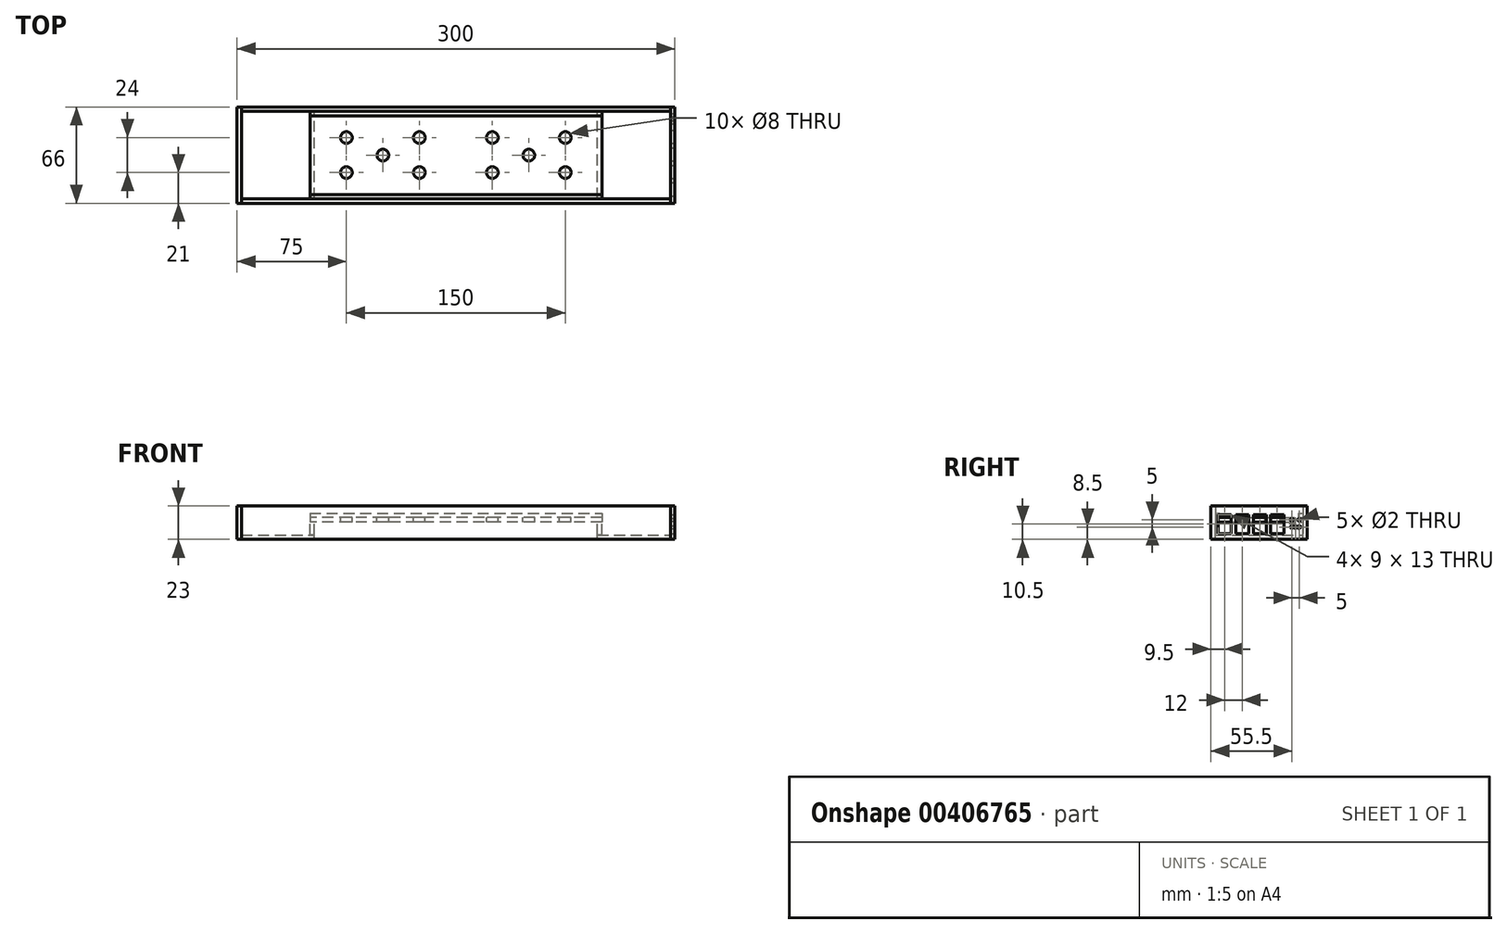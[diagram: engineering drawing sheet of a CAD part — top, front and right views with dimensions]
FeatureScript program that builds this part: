
annotation { "Feature Type Name" : "Feature", "Feature Type Description" : "" }
export const myFeature = defineFeature(function(context is Context, id is Id, definition is map)
    precondition{}
    {
        {
            var Q0;
            Q0=qCreatedBy(makeId("Top.planeOp"),FACE);
            var sketch = newSketch(context, id + "F0", { "sketchPlane" : qUnion([Q0])});
            skLineSegment(sketch, "E0.bottom", {"start": v(100, -30) * mm, "end": v(-100, -30) * mm});
            skLineSegment(sketch, "E0.top", {"start": v(100, 30) * mm, "end": v(-100, 30) * mm});
            skLineSegment(sketch, "E0.left", {"start": v(100, -30) * mm, "end": v(100, 30) * mm});
            skLineSegment(sketch, "E0.right", {"start": v(-100, -30) * mm, "end": v(-100, 30) * mm});
            skPoint(sketch, "E0.middle", {"position": v(0, 0) * mm});
            skSolve(sketch);
        }
        {
            var Q0;
            Q0=makeQuery(id+"F0.imprint","IMPRINT",FACE,{"disambiguationData":[TD([[makeQuery(id+"F0.imprint","IMPRINT",EDGE,{"derivedFrom":sQuery(id+"F0.wireOp",EDGE,"E0.bottom")}),-1.0]])]});
            extrude(context, id + "F1", {"entities" : qUnion([Q0]), "depth" : 3 * mm});
        }
        {
            var Q0;
            Q0=makeQuery(id+"F1.opExtrude","CAP_FACE",FACE,{"disambiguationData":[OSD([sQuery(id+"F0.wireOp",EDGE,"E0.bottom"),sQuery(id+"F0.wireOp",EDGE,"E0.top"),sQuery(id+"F0.wireOp",EDGE,"E0.left"),sQuery(id+"F0.wireOp",EDGE,"E0.right")])],"isStart":true});
            var sketch = newSketch(context, id + "F2", { "sketchPlane" : qUnion([Q0])});
            skLineSegment(sketch, "E1", {"start": v(-97, 30) * mm, "end": v(-97, -30) * mm});
            skLineSegment(sketch, "E2", {"start": v(97, 30) * mm, "end": v(97, -30) * mm});
            skSolve(sketch);
        }
        {
            var Q0;
            {var subQ0=sQuery(id+"F2.wireOp",EDGE,"E1");Q0=makeQuery(id+"F2.imprint","IMPRINT",FACE,{"disambiguationData":[TD([[makeQuery(id+"F2.imprint","IMPRINT",EDGE,{"derivedFrom":subQ0}),-1.0]])]});}
            var Q1;
            {var subQ0=sQuery(id+"F2.wireOp",EDGE,"E2");Q1=makeQuery(id+"F2.imprint","IMPRINT",FACE,{"disambiguationData":[TD([[makeQuery(id+"F2.imprint","IMPRINT",EDGE,{"derivedFrom":subQ0}),1.0]])]});}
            extrude(context, id + "F3", {"entities" : qUnion([Q0, Q1]), "depth" : 9 * mm});
        }
        {
            var Q0;
            Q0=makeQuery(id+"F3.opExtrude","CAP_FACE",FACE,{"disambiguationData":[OSD([sQuery(id+"F0.wireOp",EDGE,"E0.bottom"),sQuery(id+"F0.wireOp",EDGE,"E0.top"),sQuery(id+"F0.wireOp",EDGE,"E0.left"),sQuery(id+"F2.wireOp",EDGE,"E2")])],"isStart":false});
            var sketch = newSketch(context, id + "F4", { "sketchPlane" : qUnion([Q0])});
            skLineSegment(sketch, "E3", {"start": v(97, 30) * mm, "end": v(147, 30) * mm});
            skLineSegment(sketch, "E4", {"start": v(147, 30) * mm, "end": v(147, -30) * mm});
            skLineSegment(sketch, "E5", {"start": v(147, -30) * mm, "end": v(97, -30) * mm});
            skSolve(sketch);
        }
        {
            var Q0;
            {var subQ2=sQuery(id+"F4.wireOp",EDGE,"E4");Q0=makeQuery(id+"F4.imprint","IMPRINT",FACE,{"disambiguationData":[TD([[makeQuery(id+"F4.imprint","IMPRINT",EDGE,{"derivedFrom":subQ2}),-1.0]])]});}
            var Q1;
            {var subQ2=makeQuery(id+"F3.opExtrude","CAP_EDGE",EDGE,{"disambiguationData":[OSD([sQuery(id+"F2.wireOp",EDGE,"E2")])],"isStart":false});Q1=makeQuery(id+"F4.imprint","IMPRINT",FACE,{"disambiguationData":[TD([[makeQuery(id+"F4.imprint","IMPRINT",EDGE,{"derivedFrom":subQ2}),1.0]])]});}
            extrude(context, id + "F5", {"entities" : qUnion([Q0, Q1]), "depth" : 3 * mm});
        }
        {
            var Q0;
            Q0=makeQuery(id+"F3.opExtrude","CAP_FACE",FACE,{"disambiguationData":[OSD([sQuery(id+"F0.wireOp",EDGE,"E0.bottom"),sQuery(id+"F0.wireOp",EDGE,"E0.top"),sQuery(id+"F0.wireOp",EDGE,"E0.right"),sQuery(id+"F2.wireOp",EDGE,"E1")])],"isStart":false});
            var sketch = newSketch(context, id + "F6", { "sketchPlane" : qUnion([Q0])});
            skLineSegment(sketch, "E6", {"start": v(-97, 30) * mm, "end": v(-147, 30) * mm});
            skLineSegment(sketch, "E7", {"start": v(-147, 30) * mm, "end": v(-147, -30) * mm});
            skLineSegment(sketch, "E8", {"start": v(-147, -30) * mm, "end": v(-97, -30) * mm});
            skSolve(sketch);
        }
        {
            var Q0;
            {var subQ2=sQuery(id+"F6.wireOp",EDGE,"E7");Q0=makeQuery(id+"F6.imprint","IMPRINT",FACE,{"disambiguationData":[TD([[makeQuery(id+"F6.imprint","IMPRINT",EDGE,{"derivedFrom":subQ2}),1.0]])]});}
            var Q1;
            {var subQ2=makeQuery(id+"F3.opExtrude","CAP_EDGE",EDGE,{"disambiguationData":[OSD([sQuery(id+"F2.wireOp",EDGE,"E1")])],"isStart":false});Q1=makeQuery(id+"F6.imprint","IMPRINT",FACE,{"disambiguationData":[TD([[makeQuery(id+"F6.imprint","IMPRINT",EDGE,{"derivedFrom":subQ2}),-1.0]])]});}
            extrude(context, id + "F7", {"entities" : qUnion([Q0, Q1]), "depth" : 3 * mm});
        }
        {
            var Q0;
            Q0=makeQuery(id+"F1.opExtrude","CAP_FACE",FACE,{"disambiguationData":[OSD([sQuery(id+"F0.wireOp",EDGE,"E0.bottom"),sQuery(id+"F0.wireOp",EDGE,"E0.top"),sQuery(id+"F0.wireOp",EDGE,"E0.left"),sQuery(id+"F0.wireOp",EDGE,"E0.right")])],"isStart":false});
            var sketch = newSketch(context, id + "F8", { "sketchPlane" : qUnion([Q0])});
            skLineSegment(sketch, "E9", {"start": v(-100, 27) * mm, "end": v(100, 27) * mm});
            skLineSegment(sketch, "E10", {"start": v(-100, -27) * mm, "end": v(100, -27) * mm});
            skSolve(sketch);
        }
        {
            var Q0;
            {var subQ0=sQuery(id+"F8.wireOp",EDGE,"E9");Q0=makeQuery(id+"F8.imprint","IMPRINT",FACE,{"disambiguationData":[TD([[makeQuery(id+"F8.imprint","IMPRINT",EDGE,{"derivedFrom":subQ0}),1.0]])]});}
            var Q1;
            {var subQ0=sQuery(id+"F8.wireOp",EDGE,"E10");Q1=makeQuery(id+"F8.imprint","IMPRINT",FACE,{"disambiguationData":[TD([[makeQuery(id+"F8.imprint","IMPRINT",EDGE,{"derivedFrom":subQ0}),-1.0]])]});}
            extrude(context, id + "F9", {"entities" : qUnion([Q0, Q1]), "depth" : 3 * mm});
        }
        {
            var Q0;
            Q0=makeQuery(id+"F1.opExtrude","CAP_FACE",FACE,{"disambiguationData":[OSD([sQuery(id+"F0.wireOp",EDGE,"E0.bottom"),sQuery(id+"F0.wireOp",EDGE,"E0.top"),sQuery(id+"F0.wireOp",EDGE,"E0.left"),sQuery(id+"F0.wireOp",EDGE,"E0.right")])],"isStart":false});
            var sketch = newSketch(context, id + "F10", { "sketchPlane" : qUnion([Q0])});
            skLineSegment(sketch, "E11", {"start": v(0, 30) * mm, "end": v(0, -30) * mm, "construction": true});
            skLineSegment(sketch, "E12", {"start": v(-100, 0) * mm, "end": v(100, 0) * mm, "construction": true});
            skLineSegment(sketch, "E13", {"start": v(-25, 30) * mm, "end": v(-25, -30) * mm, "construction": true});
            skLineSegment(sketch, "E14", {"start": v(-75, 30) * mm, "end": v(-75, -30) * mm, "construction": true});
            skLineSegment(sketch, "E15", {"start": v(25, 30) * mm, "end": v(25, -30) * mm, "construction": true});
            skLineSegment(sketch, "E16", {"start": v(75, 30) * mm, "end": v(75, -30) * mm, "construction": true});
            skLineSegment(sketch, "E17", {"start": v(-100, 12) * mm, "end": v(100, 12) * mm, "construction": true});
            skLineSegment(sketch, "E18", {"start": v(-100, -12) * mm, "end": v(100, -12) * mm, "construction": true});
            skLineSegment(sketch, "E19", {"start": v(50, 30) * mm, "end": v(50, -30) * mm, "construction": true});
            skCircle(sketch, "E20", {"center": v(-75, 12) * mm, "radius": 10 * mm, "construction": true});
            skCircle(sketch, "E21", {"center": v(-75, -12) * mm, "radius": 10 * mm, "construction": true});
            skCircle(sketch, "E22", {"center": v(-50, 0) * mm, "radius": 10 * mm, "construction": true});
            skCircle(sketch, "E23", {"center": v(-25, 12) * mm, "radius": 10 * mm, "construction": true});
            skCircle(sketch, "E24", {"center": v(-25, -12) * mm, "radius": 10 * mm, "construction": true});
            skCircle(sketch, "E25", {"center": v(25, 12) * mm, "radius": 10 * mm, "construction": true});
            skPoint(sketch, "E25.centerSnap0", {"position": v(25, 0) * mm});
            skCircle(sketch, "E26", {"center": v(25, -12) * mm, "radius": 10 * mm, "construction": true});
            skCircle(sketch, "E27", {"center": v(75, 12) * mm, "radius": 10 * mm, "construction": true});
            skCircle(sketch, "E28", {"center": v(75, -12) * mm, "radius": 10 * mm, "construction": true});
            skCircle(sketch, "E29", {"center": v(50, 0) * mm, "radius": 10 * mm, "construction": true});
            skCircle(sketch, "E30", {"center": v(75, 12) * mm, "radius": 4 * mm});
            skCircle(sketch, "E31", {"center": v(75, -12) * mm, "radius": 4 * mm});
            skCircle(sketch, "E32", {"center": v(50, 0) * mm, "radius": 4 * mm});
            skCircle(sketch, "E33", {"center": v(25, 12) * mm, "radius": 4 * mm});
            skCircle(sketch, "E34", {"center": v(25, -12) * mm, "radius": 4 * mm});
            skCircle(sketch, "E35", {"center": v(-25, 12) * mm, "radius": 4 * mm});
            skCircle(sketch, "E36", {"center": v(-25, -12) * mm, "radius": 4 * mm});
            skCircle(sketch, "E37", {"center": v(-50, 0) * mm, "radius": 4 * mm});
            skCircle(sketch, "E38", {"center": v(-75, 12) * mm, "radius": 4 * mm});
            skCircle(sketch, "E39", {"center": v(-75, -12) * mm, "radius": 4 * mm});
            skLineSegment(sketch, "E40", {"start": v(-50, 30) * mm, "end": v(-50, -30) * mm, "construction": true});
            skSolve(sketch);
        }
        {
            var Q0;
            Q0=makeQuery(id+"F10.imprint","IMPRINT",FACE,{"disambiguationData":[TD([[makeQuery(id+"F10.imprint","IMPRINT",EDGE,{"derivedFrom":sQuery(id+"F10.wireOp",EDGE,"E38")}),1.0]])]});
            var Q1;
            Q1=makeQuery(id+"F10.imprint","IMPRINT",FACE,{"disambiguationData":[TD([[makeQuery(id+"F10.imprint","IMPRINT",EDGE,{"derivedFrom":sQuery(id+"F10.wireOp",EDGE,"E39")}),1.0]])]});
            var Q2;
            Q2=makeQuery(id+"F10.imprint","IMPRINT",FACE,{"disambiguationData":[TD([[makeQuery(id+"F10.imprint","IMPRINT",EDGE,{"derivedFrom":sQuery(id+"F10.wireOp",EDGE,"E36")}),1.0]])]});
            var Q3;
            Q3=makeQuery(id+"F10.imprint","IMPRINT",FACE,{"disambiguationData":[TD([[makeQuery(id+"F10.imprint","IMPRINT",EDGE,{"derivedFrom":sQuery(id+"F10.wireOp",EDGE,"E35")}),1.0]])]});
            var Q4;
            Q4=makeQuery(id+"F10.imprint","IMPRINT",FACE,{"disambiguationData":[TD([[makeQuery(id+"F10.imprint","IMPRINT",EDGE,{"derivedFrom":sQuery(id+"F10.wireOp",EDGE,"E33")}),1.0]])]});
            var Q5;
            Q5=makeQuery(id+"F10.imprint","IMPRINT",FACE,{"disambiguationData":[TD([[makeQuery(id+"F10.imprint","IMPRINT",EDGE,{"derivedFrom":sQuery(id+"F10.wireOp",EDGE,"E34")}),1.0]])]});
            var Q6;
            Q6=makeQuery(id+"F10.imprint","IMPRINT",FACE,{"disambiguationData":[TD([[makeQuery(id+"F10.imprint","IMPRINT",EDGE,{"derivedFrom":sQuery(id+"F10.wireOp",EDGE,"E32")}),1.0]])]});
            var Q7;
            Q7=makeQuery(id+"F10.imprint","IMPRINT",FACE,{"disambiguationData":[TD([[makeQuery(id+"F10.imprint","IMPRINT",EDGE,{"derivedFrom":sQuery(id+"F10.wireOp",EDGE,"E30")}),1.0]])]});
            var Q8;
            Q8=makeQuery(id+"F10.imprint","IMPRINT",FACE,{"disambiguationData":[TD([[makeQuery(id+"F10.imprint","IMPRINT",EDGE,{"derivedFrom":sQuery(id+"F10.wireOp",EDGE,"E31")}),1.0]])]});
            var Q9;
            {var subQ0=sQuery(id+"F10.wireOp",EDGE,"E37");var subQ1=sQuery(id+"F10.wireOp",EDGE,"U7lCM9GL-lPuP-iNZp-IQAg-3zTcT3e2uVGl");var subQ2=makeQuery(id+"F10.imprint","INTERSECT",VERTEX,{"disambiguationData":[OD(0.0)],"derivedFrom":[subQ1,subQ0]});Q9=makeQuery(id+"F10.imprint","IMPRINT",FACE,{"disambiguationData":[TD([[makeQuery(id+"F10.imprint","IMPRINT",EDGE,{"disambiguationData":[TD([[subQ2,-1.0]])],"derivedFrom":subQ1}),1.0]])]});}
            var Q10;
            {var subQ0=sQuery(id+"F10.wireOp",EDGE,"E37");var subQ1=sQuery(id+"F10.wireOp",EDGE,"U7lCM9GL-lPuP-iNZp-IQAg-3zTcT3e2uVGl");var subQ2=makeQuery(id+"F10.imprint","INTERSECT",VERTEX,{"disambiguationData":[OD(0.0)],"derivedFrom":[subQ1,subQ0]});Q10=makeQuery(id+"F10.imprint","IMPRINT",FACE,{"disambiguationData":[TD([[makeQuery(id+"F10.imprint","IMPRINT",EDGE,{"disambiguationData":[TD([[subQ2,-1.0]])],"derivedFrom":subQ1}),-1.0]])]});}
            var Q11;
            Q11=makeQuery(id+"F10.imprint","IMPRINT",FACE,{"disambiguationData":[TD([[makeQuery(id+"F10.imprint","IMPRINT",EDGE,{"derivedFrom":sQuery(id+"F10.wireOp",EDGE,"E37")}),1.0]])]});
            extrude(context, id + "F11", {"entities" : qUnion([Q0, Q1, Q2, Q3, Q4, Q5, Q6, Q7, Q8, Q9, Q10, Q11]), "operationType" : NewBodyOperationType.REMOVE, "oppositeDirection" : true, "depth" : 3 * mm});
        }
        {
            var Q0;
            Q0=makeQuery(id+"F1.opExtrude","SWEPT_FACE",FACE,{"disambiguationData":[OSD([sQuery(id+"F0.wireOp",EDGE,"E0.bottom")])]});
            var sketch = newSketch(context, id + "F12", { "sketchPlane" : qUnion([Q0])});
            skLineSegment(sketch, "E41.bottom", {"start": v(-147, 11) * mm, "end": v(147, 11) * mm});
            skLineSegment(sketch, "E41.top", {"start": v(-147, -12) * mm, "end": v(147, -12) * mm});
            skLineSegment(sketch, "E41.left", {"start": v(-147, 11) * mm, "end": v(-147, -12) * mm});
            skLineSegment(sketch, "E41.right", {"start": v(147, 11) * mm, "end": v(147, -12) * mm});
            skLineSegment(sketch, "E42", {"start": v(0, 28.89) * mm, "end": v(0, -38.06) * mm, "construction": true});
            skPoint(sketch, "E42.startSnap0", {"position": v(0, 3) * mm});
            skLineSegment(sketch, "E43", {"start": v(164.78, 0) * mm, "end": v(-162.43, 0) * mm, "construction": true});
            skPoint(sketch, "E43.startSnap0", {"position": v(0, 0) * mm});
            skPoint(sketch, "E43.endSnap0", {"position": v(0, 0) * mm});
            skSolve(sketch);
        }
        {
            var Q0;
            Q0=makeQuery(id+"F12.imprint","IMPRINT",FACE,{"disambiguationData":[TD([[makeQuery(id+"F12.imprint","IMPRINT",EDGE,{"derivedFrom":sQuery(id+"F12.wireOp",EDGE,"E41.bottom")}),-1.0]])]});
            var Q1;
            {var subQ0=sQuery(id+"F0.wireOp",EDGE,"E0.bottom");Q1=makeQuery(id+"F12.imprint","IMPRINT",FACE,{"disambiguationData":[TD([[makeQuery(id+"F12.imprint","IMPRINT",EDGE,{"derivedFrom":makeQuery(id+"F1.opExtrude","CAP_EDGE",EDGE,{"disambiguationData":[OSD([subQ0])],"isStart":true})}),-1.0]])]});}
            extrude(context, id + "F13", {"entities" : qUnion([Q0, Q1]), "depth" : 3 * mm});
        }
        {
            var Q0;
            Q0=makeQuery(id+"F1.opExtrude","SWEPT_FACE",FACE,{"disambiguationData":[OSD([sQuery(id+"F0.wireOp",EDGE,"E0.top")])]});
            var sketch = newSketch(context, id + "F14", { "sketchPlane" : qUnion([Q0])});
            skLineSegment(sketch, "E44.bottom", {"start": v(-147, 11) * mm, "end": v(147, 11) * mm});
            skLineSegment(sketch, "E44.top", {"start": v(-147, -12) * mm, "end": v(147, -12) * mm});
            skLineSegment(sketch, "E44.left", {"start": v(-147, 11) * mm, "end": v(-147, -12) * mm});
            skLineSegment(sketch, "E44.right", {"start": v(147, 11) * mm, "end": v(147, -12) * mm});
            skLineSegment(sketch, "E45", {"start": v(-168.88, 0) * mm, "end": v(173.44, 0) * mm, "construction": true});
            skPoint(sketch, "E45.startSnap0", {"position": v(0, 0) * mm});
            skLineSegment(sketch, "E46", {"start": v(0, 11) * mm, "end": v(0, -26) * mm, "construction": true});
            skPoint(sketch, "E46.endSnap0", {"position": v(0, 3) * mm});
            skSolve(sketch);
        }
        {
            var Q0;
            Q0=makeQuery(id+"F14.imprint","IMPRINT",FACE,{"disambiguationData":[TD([[makeQuery(id+"F14.imprint","IMPRINT",EDGE,{"derivedFrom":sQuery(id+"F14.wireOp",EDGE,"E44.bottom")}),-1.0]])]});
            var Q1;
            {var subQ0=sQuery(id+"F0.wireOp",EDGE,"E0.top");Q1=makeQuery(id+"F14.imprint","IMPRINT",FACE,{"disambiguationData":[TD([[makeQuery(id+"F14.imprint","IMPRINT",EDGE,{"derivedFrom":makeQuery(id+"F1.opExtrude","CAP_EDGE",EDGE,{"disambiguationData":[OSD([subQ0])],"isStart":true})}),1.0]])]});}
            extrude(context, id + "F15", {"entities" : qUnion([Q0, Q1]), "depth" : 3 * mm});
        }
        {
            var Q0;
            Q0=makeQuery(id+"F13.opExtrude","SWEPT_FACE",FACE,{"disambiguationData":[OSD([sQuery(id+"F12.wireOp",EDGE,"E41.right")])]});
            var sketch = newSketch(context, id + "F16", { "sketchPlane" : qUnion([Q0])});
            skLineSegment(sketch, "E47", {"start": v(-33, 11) * mm, "end": v(33, 11) * mm});
            skLineSegment(sketch, "E48", {"start": v(33, 11) * mm, "end": v(33, -12) * mm});
            skLineSegment(sketch, "E49", {"start": v(33, -12) * mm, "end": v(-33, -12) * mm});
            skSolve(sketch);
        }
        {
            var Q0;
            {var subQ2=sQuery(id+"F16.wireOp",EDGE,"E48");Q0=makeQuery(id+"F16.imprint","IMPRINT",FACE,{"disambiguationData":[TD([[makeQuery(id+"F16.imprint","IMPRINT",EDGE,{"derivedFrom":subQ2}),-1.0]])]});}
            var Q1;
            {var subQ1=sQuery(id+"F12.wireOp",EDGE,"E41.right");var subQ2=makeQuery(id+"F13.opExtrude","CAP_EDGE",EDGE,{"disambiguationData":[OSD([subQ1])],"isStart":true});Q1=makeQuery(id+"F16.imprint","IMPRINT",FACE,{"disambiguationData":[TD([[makeQuery(id+"F16.imprint","IMPRINT",EDGE,{"derivedFrom":subQ2}),-1.0]])]});}
            extrude(context, id + "F17", {"entities" : qUnion([Q0, Q1]), "depth" : 3 * mm});
        }
        {
            var Q0;
            Q0=makeQuery(id+"F15.opExtrude","SWEPT_FACE",FACE,{"disambiguationData":[OSD([sQuery(id+"F14.wireOp",EDGE,"E44.right")])]});
            var sketch = newSketch(context, id + "F18", { "sketchPlane" : qUnion([Q0])});
            skLineSegment(sketch, "E50", {"start": v(-33, 11) * mm, "end": v(33, 11) * mm});
            skLineSegment(sketch, "E51", {"start": v(33, 11) * mm, "end": v(33, -12) * mm});
            skLineSegment(sketch, "E52", {"start": v(33, -12) * mm, "end": v(-33, -12) * mm});
            skSolve(sketch);
        }
        {
            var Q0;
            {var subQ1=sQuery(id+"F14.wireOp",EDGE,"E44.right");var subQ2=makeQuery(id+"F15.opExtrude","CAP_EDGE",EDGE,{"disambiguationData":[OSD([subQ1])],"isStart":true});Q0=makeQuery(id+"F18.imprint","IMPRINT",FACE,{"disambiguationData":[TD([[makeQuery(id+"F18.imprint","IMPRINT",EDGE,{"derivedFrom":subQ2}),-1.0]])]});}
            var Q1;
            {var subQ2=sQuery(id+"F18.wireOp",EDGE,"E51");Q1=makeQuery(id+"F18.imprint","IMPRINT",FACE,{"disambiguationData":[TD([[makeQuery(id+"F18.imprint","IMPRINT",EDGE,{"derivedFrom":subQ2}),-1.0]])]});}
            extrude(context, id + "F19", {"entities" : qUnion([Q0, Q1]), "depth" : 3 * mm});
        }
        {
            var Q0;
            Q0=makeQuery(id+"F17.opExtrude","CAP_FACE",FACE,{"disambiguationData":[OSD([sQuery(id+"F12.wireOp",EDGE,"E41.right"),sQuery(id+"F16.wireOp",EDGE,"E47"),sQuery(id+"F16.wireOp",EDGE,"E48"),sQuery(id+"F16.wireOp",EDGE,"E49")])],"isStart":false});
            var sketch = newSketch(context, id + "F20", { "sketchPlane" : qUnion([Q0])});
            skLineSegment(sketch, "E53", {"start": v(30, 11) * mm, "end": v(30, -12) * mm, "construction": true});
            skLineSegment(sketch, "E54", {"start": v(-30, 11) * mm, "end": v(-30, -12) * mm, "construction": true});
            skLineSegment(sketch, "E55", {"start": v(-33, -9) * mm, "end": v(33, -9) * mm, "construction": true});
            skLineSegment(sketch, "E56", {"start": v(-33, -1) * mm, "end": v(33, -1) * mm, "construction": true});
            skLineSegment(sketch, "E57", {"start": v(27.5, 11) * mm, "end": v(27.5, -9) * mm, "construction": true});
            skLineSegment(sketch, "E58", {"start": v(25, 11) * mm, "end": v(25, -9) * mm, "construction": true});
            skLineSegment(sketch, "E59", {"start": v(22.5, 11) * mm, "end": v(22.5, -9) * mm, "construction": true});
            skLineSegment(sketch, "E60", {"start": v(22.5, 1.5) * mm, "end": v(27.5, 1.5) * mm, "construction": true});
            skLineSegment(sketch, "E61", {"start": v(22.5, -3.5) * mm, "end": v(27.5, -3.5) * mm, "construction": true});
            skCircle(sketch, "E62", {"center": v(22.5, 1.5) * mm, "radius": 1 * mm});
            skCircle(sketch, "E63", {"center": v(27.5, 1.5) * mm, "radius": 1 * mm});
            skCircle(sketch, "E64", {"center": v(27.5, -3.5) * mm, "radius": 1 * mm});
            skCircle(sketch, "E65", {"center": v(25, -3.5) * mm, "radius": 1 * mm});
            skCircle(sketch, "E66", {"center": v(22.5, -3.5) * mm, "radius": 1 * mm});
            skLineSegment(sketch, "E67", {"start": v(-35.7, 6) * mm, "end": v(35.77, 6) * mm, "construction": true});
            skLineSegment(sketch, "E68", {"start": v(-35.7, 5) * mm, "end": v(36.02, 5) * mm, "construction": true});
            skLineSegment(sketch, "E69", {"start": v(-35.42, -8) * mm, "end": v(35.63, -8) * mm, "construction": true});
            skLineSegment(sketch, "E70.bottom", {"start": v(-28, 5) * mm, "end": v(-19, 5) * mm});
            skLineSegment(sketch, "E70.top", {"start": v(-28, -8) * mm, "end": v(-19, -8) * mm});
            skLineSegment(sketch, "E70.left", {"start": v(-28, 5) * mm, "end": v(-28, -8) * mm});
            skLineSegment(sketch, "E70.right", {"start": v(-19, 5) * mm, "end": v(-19, -8) * mm});
            skLineSegment(sketch, "E71.bottom", {"start": v(-16, 5) * mm, "end": v(-7, 5) * mm});
            skLineSegment(sketch, "E71.top", {"start": v(-16, -8) * mm, "end": v(-7, -8) * mm});
            skLineSegment(sketch, "E71.left", {"start": v(-16, 5) * mm, "end": v(-16, -8) * mm});
            skLineSegment(sketch, "E71.right", {"start": v(-7, 5) * mm, "end": v(-7, -8) * mm});
            skLineSegment(sketch, "E72.bottom", {"start": v(-4, 5) * mm, "end": v(5, 5) * mm});
            skLineSegment(sketch, "E72.top", {"start": v(-4, -8) * mm, "end": v(5, -8) * mm});
            skLineSegment(sketch, "E72.left", {"start": v(-4, 5) * mm, "end": v(-4, -8) * mm});
            skLineSegment(sketch, "E72.right", {"start": v(5, 5) * mm, "end": v(5, -8) * mm});
            skLineSegment(sketch, "E73.bottom", {"start": v(8, 5) * mm, "end": v(17, 5) * mm});
            skLineSegment(sketch, "E73.top", {"start": v(8, -8) * mm, "end": v(17, -8) * mm});
            skLineSegment(sketch, "E73.left", {"start": v(8, 5) * mm, "end": v(8, -8) * mm});
            skLineSegment(sketch, "E73.right", {"start": v(17, 5) * mm, "end": v(17, -8) * mm});
            skSolve(sketch);
        }
        {
            var Q0;
            Q0=makeQuery(id+"F20.imprint","IMPRINT",FACE,{"disambiguationData":[TD([[makeQuery(id+"F20.imprint","IMPRINT",EDGE,{"derivedFrom":sQuery(id+"F20.wireOp",EDGE,"E70.bottom")}),-1.0]])]});
            var Q1;
            Q1=makeQuery(id+"F20.imprint","IMPRINT",FACE,{"disambiguationData":[TD([[makeQuery(id+"F20.imprint","IMPRINT",EDGE,{"derivedFrom":sQuery(id+"F20.wireOp",EDGE,"E71.bottom")}),-1.0]])]});
            var Q2;
            Q2=makeQuery(id+"F20.imprint","IMPRINT",FACE,{"disambiguationData":[TD([[makeQuery(id+"F20.imprint","IMPRINT",EDGE,{"derivedFrom":sQuery(id+"F20.wireOp",EDGE,"E72.bottom")}),-1.0]])]});
            var Q3;
            Q3=makeQuery(id+"F20.imprint","IMPRINT",FACE,{"disambiguationData":[TD([[makeQuery(id+"F20.imprint","IMPRINT",EDGE,{"derivedFrom":sQuery(id+"F20.wireOp",EDGE,"E73.bottom")}),-1.0]])]});
            var Q4;
            Q4=makeQuery(id+"F20.imprint","IMPRINT",FACE,{"disambiguationData":[TD([[makeQuery(id+"F20.imprint","IMPRINT",EDGE,{"derivedFrom":sQuery(id+"F20.wireOp",EDGE,"E62")}),1.0]])]});
            var Q5;
            Q5=makeQuery(id+"F20.imprint","IMPRINT",FACE,{"disambiguationData":[TD([[makeQuery(id+"F20.imprint","IMPRINT",EDGE,{"derivedFrom":sQuery(id+"F20.wireOp",EDGE,"E63")}),1.0]])]});
            var Q6;
            Q6=makeQuery(id+"F20.imprint","IMPRINT",FACE,{"disambiguationData":[TD([[makeQuery(id+"F20.imprint","IMPRINT",EDGE,{"derivedFrom":sQuery(id+"F20.wireOp",EDGE,"E64")}),1.0]])]});
            var Q7;
            Q7=makeQuery(id+"F20.imprint","IMPRINT",FACE,{"disambiguationData":[TD([[makeQuery(id+"F20.imprint","IMPRINT",EDGE,{"derivedFrom":sQuery(id+"F20.wireOp",EDGE,"E65")}),1.0]])]});
            var Q8;
            Q8=makeQuery(id+"F20.imprint","IMPRINT",FACE,{"disambiguationData":[TD([[makeQuery(id+"F20.imprint","IMPRINT",EDGE,{"derivedFrom":sQuery(id+"F20.wireOp",EDGE,"E66")}),1.0]])]});
            extrude(context, id + "F21", {"entities" : qUnion([Q0, Q1, Q2, Q3, Q4, Q5, Q6, Q7, Q8]), "operationType" : NewBodyOperationType.REMOVE, "oppositeDirection" : true, "depth" : 25 * mm});
        }
    });
